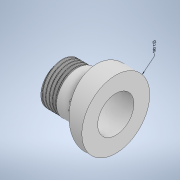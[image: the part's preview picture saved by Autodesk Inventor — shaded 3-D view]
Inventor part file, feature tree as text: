
AUTODESK INVENTOR PART (.ipt)
format: ipt  version: 2021.1 (Build 251245010, 245A)  size: 793,600 bytes
history: native  units: in
note: dims shown in document units (in); Inventor stores cm internally (conversion verified against a paired STEP export)
features: sketch x4, plane x3, other x2, revolve x1, helix x1, emboss x1, extrude x1
ambient origin geometry x8: Origin, YZ Plane, XZ Plane, XY Plane, X Axis, Y Axis, Z Axis, Center Point
bodies: Solid1 (feature_tree)
feature tree (13):
  other  "Annotations"
  revolve  "Revolution1"  [1 undecoded]
  helix  "Coil1"  [1 undecoded]
  plane  "Work Plane2"
  emboss  "Emboss2"
  plane  "Work Plane4"
  extrude  "Extrusion1"  TaperAngle=90.0deg  [1 undecoded]
  sketch  "Sketch2"  dims[d0=1.0in d1=0.5344in d2=0.125in]
  sketch  "Sketch4"  dims[d3=1.25in d4=90.0deg]
  sketch  "Sketch6"  dims[d5=0.625in]
  plane  "Work Plane3"
  sketch  "Sketch8"  dims[d6=0.25in d10=60.0deg d11=0.0072in d12=60.0deg d13=60.0deg d15=0.1in d16=0.2in d17=0.05in d18=0.6144in d19=0.5494in d20=30.0deg d21=0.1in d22=0.625in d23=0.3937in d24=0.0in d25=90.0deg d26=90.0deg d27=0.0in d28=0.0in d38=0.0906in d39=0.5494in d40=0.6144in d41=0.25in d42=0.05in d43=0.0in d44=0.0825in d45=0.35in d46=1.0in d47=0.0in d48=1.9814in d49=2.0in]
  other  "Diameter Dimension 1"
note: 3 required parameter values undecoded (feature->parameter linkage not recoverable at this tier; creation-order binding heuristic only, values carry confidence <= 0.55)